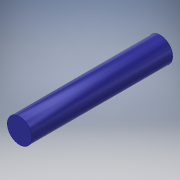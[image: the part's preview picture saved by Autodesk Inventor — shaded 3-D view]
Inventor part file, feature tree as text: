
AUTODESK INVENTOR PART (.ipt)
format: ipt  version: 2019 (Build 230136000, 136)  size: 99,840 bytes
history: native  units: mm
features: extrude x1, sketch x1
ambient origin geometry x8: Origin, YZ Plane, XZ Plane, XY Plane, X Axis, Y Axis, Z Axis, Center Point
bodies: Solid1 (feature_tree)
feature tree (2):
  extrude  "Extrusion1"  Depth=20.0mm TaperAngle=0.0deg
  sketch  "Sketch1"  dims[d0=3.5mm d1=20.0mm d2=0.0mm]
